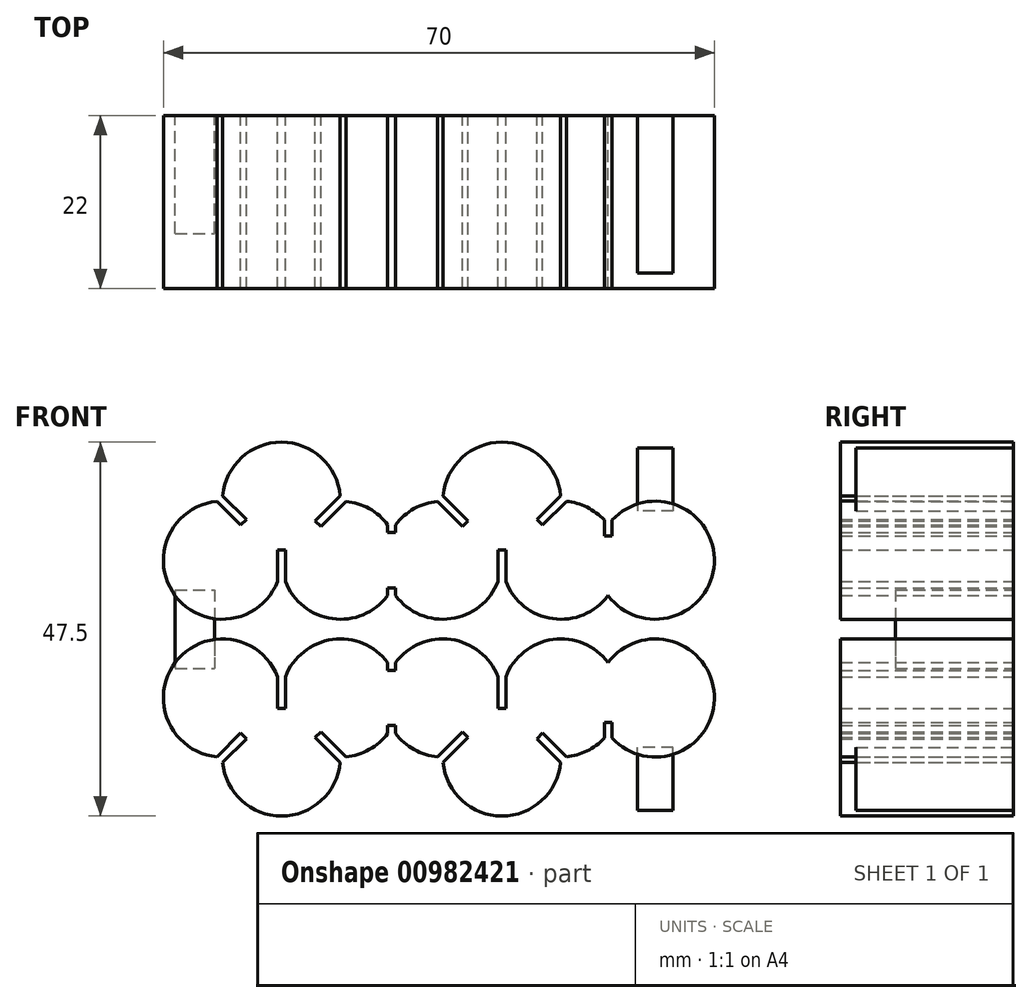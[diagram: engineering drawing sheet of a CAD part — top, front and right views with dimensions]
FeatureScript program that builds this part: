
annotation { "Feature Type Name" : "Feature", "Feature Type Description" : "" }
export const myFeature = defineFeature(function(context is Context, id is Id, definition is map)
    precondition{}
    {
        {
            var Q0;
            Q0=qCreatedBy(makeId("Front.planeOp"),FACE);
            var sketch = newSketch(context, id + "F0", { "sketchPlane" : qUnion([Q0])});
            skLineSegment(sketch, "E0.bottom", {"start": v(0, -25) * mm, "end": v(76, -25) * mm});
            skLineSegment(sketch, "E0.top", {"start": v(0, 25) * mm, "end": v(76, 25) * mm});
            skLineSegment(sketch, "E0.left", {"start": v(0, -25) * mm, "end": v(0, 25) * mm});
            skLineSegment(sketch, "E0.right", {"start": v(76, -25) * mm, "end": v(76, 25) * mm});
            skSolve(sketch);
        }
        {
            var Q0;
            Q0=makeQuery(id+"F0.imprint","IMPRINT",FACE,{"disambiguationData":[TD([[makeQuery(id+"F0.imprint","IMPRINT",EDGE,{"derivedFrom":sQuery(id+"F0.wireOp",EDGE,"E0.bottom")}),1.0]])]});
            var sketch = newSketch(context, id + "F1", { "sketchPlane" : qUnion([Q0])});
            skArc(sketch, "E1", {"start": v(10.03, -16.93) * mm, "mid": v(17.5, -23.75) * mm, "end": v(24.97, -16.93) * mm});
            skArc(sketch, "E2", {"start": v(25.68, -16.22) * mm, "mid": v(28.65, -15.3) * mm, "end": v(31, -13.25) * mm});
            skLineSegment(sketch, "E3.0", {"start": v(10.03, -16.93) * mm, "end": v(13.04, -13.92) * mm});
            skLineSegment(sketch, "E4.0", {"start": v(9.32, -16.22) * mm, "end": v(12.33, -13.21) * mm});
            skLineSegment(sketch, "E5.0", {"start": v(12.33, -13.21) * mm, "end": v(13.04, -13.92) * mm});
            skLineSegment(sketch, "E6.0", {"start": v(22.5, -13.04) * mm, "end": v(21.79, -13.74) * mm});
            skLineSegment(sketch, "E7.trimOffspring", {"start": v(21.79, -13.74) * mm, "end": v(24.97, -16.93) * mm});
            skLineSegment(sketch, "E8.trimOffspring", {"start": v(22.5, -13.04) * mm, "end": v(25.68, -16.22) * mm});
            skArc(sketch, "E9.trimOffspring", {"start": v(17, -6.06) * mm, "mid": v(4.02, -4.23) * mm, "end": v(9.32, -16.22) * mm});
            skLineSegment(sketch, "E10.0", {"start": v(18, -10.06) * mm, "end": v(18, -6.06) * mm});
            skLineSegment(sketch, "E11.0", {"start": v(17, -10.06) * mm, "end": v(17, -6.06) * mm});
            skLineSegment(sketch, "E12.0", {"start": v(17, -10.06) * mm, "end": v(18, -10.06) * mm});
            skArc(sketch, "E13", {"start": v(32, -13.25) * mm, "mid": v(34.35, -15.3) * mm, "end": v(37.32, -16.22) * mm});
            skLineSegment(sketch, "E14.0", {"start": v(31, -4.25) * mm, "end": v(31, -5.25) * mm});
            skLineSegment(sketch, "E15.0", {"start": v(32, -4.25) * mm, "end": v(32, -5.25) * mm});
            skArc(sketch, "E16.trimOffspring", {"start": v(31, -4.25) * mm, "mid": v(23.97, -1.32) * mm, "end": v(18, -6.06) * mm});
            skLineSegment(sketch, "E17.0", {"start": v(31, -5.25) * mm, "end": v(32, -5.25) * mm});
            skLineSegment(sketch, "E18.0", {"start": v(31, -12.25) * mm, "end": v(32, -12.25) * mm});
            skLineSegment(sketch, "E19.trimOffspring", {"start": v(31, -12.25) * mm, "end": v(31, -13.25) * mm});
            skLineSegment(sketch, "E20.trimOffspring", {"start": v(32, -12.25) * mm, "end": v(32, -13.25) * mm});
            skArc(sketch, "E21", {"start": v(38.03, -16.93) * mm, "mid": v(45.5, -23.75) * mm, "end": v(52.97, -16.93) * mm});
            skLineSegment(sketch, "E22.0", {"start": v(38.03, -16.93) * mm, "end": v(41.21, -13.74) * mm});
            skLineSegment(sketch, "E23.0", {"start": v(37.32, -16.22) * mm, "end": v(40.5, -13.04) * mm});
            skLineSegment(sketch, "E24.0", {"start": v(50.67, -13.21) * mm, "end": v(53.68, -16.22) * mm});
            skArc(sketch, "E25.trimOffspring", {"start": v(53.68, -16.22) * mm, "mid": v(56.3, -15.48) * mm, "end": v(58.5, -13.85) * mm});
            skArc(sketch, "E26.trimOffspring", {"start": v(45, -6.06) * mm, "mid": v(39.03, -1.32) * mm, "end": v(32, -4.25) * mm});
            skLineSegment(sketch, "E27.0", {"start": v(40.5, -13.04) * mm, "end": v(41.21, -13.74) * mm});
            skLineSegment(sketch, "E28.0", {"start": v(49.96, -13.92) * mm, "end": v(50.67, -13.21) * mm});
            skLineSegment(sketch, "E29.trimOffspring", {"start": v(49.96, -13.92) * mm, "end": v(52.97, -16.93) * mm});
            skLineSegment(sketch, "E30.0", {"start": v(46, -10.06) * mm, "end": v(46, -6.06) * mm});
            skLineSegment(sketch, "E31.0", {"start": v(45, -10.06) * mm, "end": v(45, -6.06) * mm});
            skLineSegment(sketch, "E32.0", {"start": v(45, -10.06) * mm, "end": v(46, -10.06) * mm});
            skArc(sketch, "E33", {"start": v(59.5, -13.85) * mm, "mid": v(72.49, -8.36) * mm, "end": v(59, -4.25) * mm});
            skLineSegment(sketch, "E34.0", {"start": v(59.5, -13.85) * mm, "end": v(59.5, -11.85) * mm});
            skLineSegment(sketch, "E35.0", {"start": v(58.5, -13.85) * mm, "end": v(58.5, -11.85) * mm});
            skLineSegment(sketch, "E36.0", {"start": v(58.5, -11.85) * mm, "end": v(59.5, -11.85) * mm});
            skArc(sketch, "E37.trimOffspring", {"start": v(59, -4.25) * mm, "mid": v(51.97, -1.32) * mm, "end": v(46, -6.06) * mm});
            skLineSegment(sketch, "E38.MirrorCS", {"start": v(31, 12.25) * mm, "end": v(32, 12.25) * mm});
            skLineSegment(sketch, "E39.MirrorCS", {"start": v(31, 5.25) * mm, "end": v(32, 5.25) * mm});
            skLineSegment(sketch, "E40.MirrorCS", {"start": v(49.96, 13.92) * mm, "end": v(50.67, 13.21) * mm});
            skLineSegment(sketch, "E41.MirrorCS", {"start": v(59.5, 13.85) * mm, "end": v(59.5, 11.85) * mm});
            skLineSegment(sketch, "E42.MirrorCS", {"start": v(12.33, 13.21) * mm, "end": v(13.04, 13.92) * mm});
            skLineSegment(sketch, "E43.MirrorCS", {"start": v(32, 12.25) * mm, "end": v(32, 13.25) * mm});
            skLineSegment(sketch, "E44.MirrorCS", {"start": v(22.5, 13.04) * mm, "end": v(21.79, 13.74) * mm});
            skLineSegment(sketch, "E45.MirrorCS", {"start": v(31, 12.25) * mm, "end": v(31, 13.25) * mm});
            skLineSegment(sketch, "E46.MirrorCS", {"start": v(58.5, 11.85) * mm, "end": v(59.5, 11.85) * mm});
            skLineSegment(sketch, "E47.MirrorCS", {"start": v(32, 4.25) * mm, "end": v(32, 5.25) * mm});
            skLineSegment(sketch, "E48.MirrorCS", {"start": v(17, 10.06) * mm, "end": v(18, 10.06) * mm});
            skLineSegment(sketch, "E49.MirrorCS", {"start": v(45, 10.06) * mm, "end": v(46, 10.06) * mm});
            skLineSegment(sketch, "E50.MirrorCS", {"start": v(58.5, 13.85) * mm, "end": v(58.5, 11.85) * mm});
            skLineSegment(sketch, "E51.MirrorCS", {"start": v(40.5, 13.04) * mm, "end": v(41.21, 13.74) * mm});
            skLineSegment(sketch, "E52.MirrorCS", {"start": v(31, 4.25) * mm, "end": v(31, 5.25) * mm});
            skLineSegment(sketch, "E53.MirrorCS", {"start": v(22.5, 13.04) * mm, "end": v(25.68, 16.22) * mm});
            skLineSegment(sketch, "E54.MirrorCS", {"start": v(45, 10.06) * mm, "end": v(45, 6.06) * mm});
            skArc(sketch, "E55.MirrorCS", {"start": v(38.03, 16.93) * mm, "mid": v(45.5, 23.75) * mm, "end": v(52.97, 16.93) * mm});
            skLineSegment(sketch, "E56.MirrorCS", {"start": v(17, 10.06) * mm, "end": v(17, 6.06) * mm});
            skArc(sketch, "E57.MirrorCS", {"start": v(45, 6.06) * mm, "mid": v(39.03, 1.32) * mm, "end": v(32, 4.25) * mm});
            skArc(sketch, "E58.MirrorCS", {"start": v(32, 13.25) * mm, "mid": v(34.35, 15.3) * mm, "end": v(37.32, 16.22) * mm});
            skArc(sketch, "E59.MirrorCS", {"start": v(17, 6.06) * mm, "mid": v(4.02, 4.23) * mm, "end": v(9.32, 16.22) * mm});
            skLineSegment(sketch, "E60.MirrorCS", {"start": v(18, 10.06) * mm, "end": v(18, 6.06) * mm});
            skLineSegment(sketch, "E61.MirrorCS", {"start": v(10.03, 16.93) * mm, "end": v(13.04, 13.92) * mm});
            skLineSegment(sketch, "E62.MirrorCS", {"start": v(21.79, 13.74) * mm, "end": v(24.97, 16.93) * mm});
            skLineSegment(sketch, "E63.MirrorCS", {"start": v(37.32, 16.22) * mm, "end": v(40.5, 13.04) * mm});
            skArc(sketch, "E64.MirrorCS", {"start": v(59.5, 13.85) * mm, "mid": v(72.49, 8.36) * mm, "end": v(59, 4.25) * mm});
            skLineSegment(sketch, "E65.MirrorCS", {"start": v(46, 10.06) * mm, "end": v(46, 6.06) * mm});
            skArc(sketch, "E66.MirrorCS", {"start": v(53.68, 16.22) * mm, "mid": v(56.3, 15.48) * mm, "end": v(58.5, 13.85) * mm});
            skLineSegment(sketch, "E67.MirrorCS", {"start": v(9.32, 16.22) * mm, "end": v(12.33, 13.21) * mm});
            skArc(sketch, "E68.MirrorCS", {"start": v(59, 4.25) * mm, "mid": v(51.97, 1.32) * mm, "end": v(46, 6.06) * mm});
            skArc(sketch, "E69.MirrorCS", {"start": v(25.68, 16.22) * mm, "mid": v(28.65, 15.3) * mm, "end": v(31, 13.25) * mm});
            skArc(sketch, "E70.MirrorCS", {"start": v(31, 4.25) * mm, "mid": v(23.97, 1.32) * mm, "end": v(18, 6.06) * mm});
            skLineSegment(sketch, "E71.MirrorCS", {"start": v(50.67, 13.21) * mm, "end": v(53.68, 16.22) * mm});
            skLineSegment(sketch, "E72.MirrorCS", {"start": v(49.96, 13.92) * mm, "end": v(52.97, 16.93) * mm});
            skLineSegment(sketch, "E73.MirrorCS", {"start": v(38.03, 16.93) * mm, "end": v(41.21, 13.74) * mm});
            skArc(sketch, "E74.MirrorCS", {"start": v(10.03, 16.93) * mm, "mid": v(17.5, 23.75) * mm, "end": v(24.97, 16.93) * mm});
            skSolve(sketch);
        }
        {
            var Q0;
            Q0 = qSketchRegion(id + "F1", true);
            extrude(context, id + "F2", {"entities" : qUnion([Q0]), "depth" : 22 * mm, "offsetDistance" : 25 * mm});
        }
        {
            var Q0;
            Q0=makeQuery(id+"F2.opExtrude","CAP_FACE",FACE,{"disambiguationData":[OSD([sQuery(id+"F1.wireOp",EDGE,"E1"),sQuery(id+"F1.wireOp",EDGE,"E2"),sQuery(id+"F1.wireOp",EDGE,"E3.0"),sQuery(id+"F1.wireOp",EDGE,"E4.0"),sQuery(id+"F1.wireOp",EDGE,"E5.0"),sQuery(id+"F1.wireOp",EDGE,"E6.0"),sQuery(id+"F1.wireOp",EDGE,"E7.trimOffspring"),sQuery(id+"F1.wireOp",EDGE,"E8.trimOffspring"),sQuery(id+"F1.wireOp",EDGE,"E9.trimOffspring"),sQuery(id+"F1.wireOp",EDGE,"E10.0"),sQuery(id+"F1.wireOp",EDGE,"E11.0"),sQuery(id+"F1.wireOp",EDGE,"E12.0"),sQuery(id+"F1.wireOp",EDGE,"E13"),sQuery(id+"F1.wireOp",EDGE,"E14.0"),sQuery(id+"F1.wireOp",EDGE,"E15.0"),sQuery(id+"F1.wireOp",EDGE,"E16.trimOffspring"),sQuery(id+"F1.wireOp",EDGE,"E17.0"),sQuery(id+"F1.wireOp",EDGE,"E18.0"),sQuery(id+"F1.wireOp",EDGE,"E19.trimOffspring"),sQuery(id+"F1.wireOp",EDGE,"E20.trimOffspring"),sQuery(id+"F1.wireOp",EDGE,"E21"),sQuery(id+"F1.wireOp",EDGE,"E22.0"),sQuery(id+"F1.wireOp",EDGE,"E23.0"),sQuery(id+"F1.wireOp",EDGE,"E24.0"),sQuery(id+"F1.wireOp",EDGE,"E25.trimOffspring"),sQuery(id+"F1.wireOp",EDGE,"E26.trimOffspring"),sQuery(id+"F1.wireOp",EDGE,"E27.0"),sQuery(id+"F1.wireOp",EDGE,"E28.0"),sQuery(id+"F1.wireOp",EDGE,"E29.trimOffspring"),sQuery(id+"F1.wireOp",EDGE,"E30.0"),sQuery(id+"F1.wireOp",EDGE,"E31.0"),sQuery(id+"F1.wireOp",EDGE,"E32.0"),sQuery(id+"F1.wireOp",EDGE,"E33"),sQuery(id+"F1.wireOp",EDGE,"E34.0"),sQuery(id+"F1.wireOp",EDGE,"E35.0"),sQuery(id+"F1.wireOp",EDGE,"E36.0"),sQuery(id+"F1.wireOp",EDGE,"E37.trimOffspring")])],"isStart":false});
            var sketch = newSketch(context, id + "F3", { "sketchPlane" : qUnion([Q0])});
            skCircle(sketch, "E75", {"center": v(10, -8.75) * mm, "radius": 2 * mm});
            skSolve(sketch);
        }
        {
            var Q0;
            Q0=makeQuery(id+"F3.imprint","IMPRINT",FACE,{"disambiguationData":[TD([[makeQuery(id+"F3.imprint","IMPRINT",EDGE,{"derivedFrom":sQuery(id+"F3.wireOp",EDGE,"E75")}),1.0]])]});
            var Q1;
            Q1=sQuery(id+"F3.wireOp",EDGE,"E75");
            extrude(context, id + "F4", {"entities" : qUnion([Q0]), "surfaceEntities" : qUnion([Q1]), "oppositeDirection" : true, "depth" : 21 * mm, "offsetDistance" : 25 * mm});
        }
        {
            var Q0;
            Q0=makeQuery(id+"F4.opExtrude","CAP_FACE",FACE,{"disambiguationData":[OSD([sQuery(id+"F3.wireOp",EDGE,"E75")])],"isStart":false});
            var sketch = newSketch(context, id + "F5", { "sketchPlane" : qUnion([Q0])});
            skCircle(sketch, "E76", {"center": v(-10, -8.75) * mm, "radius": 4 * mm});
            skSolve(sketch);
        }
        {
            var Q0;
            Q0 = qSketchRegion(id + "F5", true);
            extrude(context, id + "F6", {"entities" : qUnion([Q0]), "operationType" : NewBodyOperationType.ADD, "oppositeDirection" : true, "depth" : 1 * mm, "offsetDistance" : 25 * mm});
        }
        {
            var Q0;
            Q0=makeQuery(id+"F2.opExtrude","CAP_FACE",FACE,{"disambiguationData":[OSD([sQuery(id+"F1.wireOp",EDGE,"E1"),sQuery(id+"F1.wireOp",EDGE,"E2"),sQuery(id+"F1.wireOp",EDGE,"E3.0"),sQuery(id+"F1.wireOp",EDGE,"E4.0"),sQuery(id+"F1.wireOp",EDGE,"E5.0"),sQuery(id+"F1.wireOp",EDGE,"E6.0"),sQuery(id+"F1.wireOp",EDGE,"E7.trimOffspring"),sQuery(id+"F1.wireOp",EDGE,"E8.trimOffspring"),sQuery(id+"F1.wireOp",EDGE,"E9.trimOffspring"),sQuery(id+"F1.wireOp",EDGE,"E10.0"),sQuery(id+"F1.wireOp",EDGE,"E11.0"),sQuery(id+"F1.wireOp",EDGE,"E12.0"),sQuery(id+"F1.wireOp",EDGE,"E13"),sQuery(id+"F1.wireOp",EDGE,"E14.0"),sQuery(id+"F1.wireOp",EDGE,"E15.0"),sQuery(id+"F1.wireOp",EDGE,"E16.trimOffspring"),sQuery(id+"F1.wireOp",EDGE,"E17.0"),sQuery(id+"F1.wireOp",EDGE,"E18.0"),sQuery(id+"F1.wireOp",EDGE,"E19.trimOffspring"),sQuery(id+"F1.wireOp",EDGE,"E20.trimOffspring"),sQuery(id+"F1.wireOp",EDGE,"E21"),sQuery(id+"F1.wireOp",EDGE,"E22.0"),sQuery(id+"F1.wireOp",EDGE,"E23.0"),sQuery(id+"F1.wireOp",EDGE,"E24.0"),sQuery(id+"F1.wireOp",EDGE,"E25.trimOffspring"),sQuery(id+"F1.wireOp",EDGE,"E26.trimOffspring"),sQuery(id+"F1.wireOp",EDGE,"E27.0"),sQuery(id+"F1.wireOp",EDGE,"E28.0"),sQuery(id+"F1.wireOp",EDGE,"E29.trimOffspring"),sQuery(id+"F1.wireOp",EDGE,"E30.0"),sQuery(id+"F1.wireOp",EDGE,"E31.0"),sQuery(id+"F1.wireOp",EDGE,"E32.0"),sQuery(id+"F1.wireOp",EDGE,"E33"),sQuery(id+"F1.wireOp",EDGE,"E34.0"),sQuery(id+"F1.wireOp",EDGE,"E35.0"),sQuery(id+"F1.wireOp",EDGE,"E36.0"),sQuery(id+"F1.wireOp",EDGE,"E37.trimOffspring")])],"isStart":false});
            var sketch = newSketch(context, id + "F7", { "sketchPlane" : qUnion([Q0])});
            skCircle(sketch, "E77", {"center": v(17.5, -16.25) * mm, "radius": 2 * mm});
            skSolve(sketch);
        }
        {
            var Q0;
            Q0 = qSketchRegion(id + "F7", true);
            extrude(context, id + "F8", {"entities" : qUnion([Q0]), "oppositeDirection" : true, "depth" : 21 * mm, "offsetDistance" : 25 * mm});
        }
        {
            var Q0;
            Q0=makeQuery(id+"F8.opExtrude","CAP_FACE",FACE,{"disambiguationData":[OSD([sQuery(id+"F7.wireOp",EDGE,"E77")])],"isStart":false});
            var sketch = newSketch(context, id + "F9", { "sketchPlane" : qUnion([Q0])});
            skCircle(sketch, "E78", {"center": v(-17.5, -16.25) * mm, "radius": 4 * mm});
            skSolve(sketch);
        }
        {
            var Q0;
            Q0 = qSketchRegion(id + "F9", true);
            extrude(context, id + "F10", {"entities" : qUnion([Q0]), "operationType" : NewBodyOperationType.ADD, "oppositeDirection" : true, "depth" : 1 * mm, "offsetDistance" : 25 * mm});
        }
        {
            var Q0;
            Q0=makeQuery(id+"F2.opExtrude","CAP_FACE",FACE,{"disambiguationData":[OSD([sQuery(id+"F1.wireOp",EDGE,"E1"),sQuery(id+"F1.wireOp",EDGE,"E2"),sQuery(id+"F1.wireOp",EDGE,"E3.0"),sQuery(id+"F1.wireOp",EDGE,"E4.0"),sQuery(id+"F1.wireOp",EDGE,"E5.0"),sQuery(id+"F1.wireOp",EDGE,"E6.0"),sQuery(id+"F1.wireOp",EDGE,"E7.trimOffspring"),sQuery(id+"F1.wireOp",EDGE,"E8.trimOffspring"),sQuery(id+"F1.wireOp",EDGE,"E9.trimOffspring"),sQuery(id+"F1.wireOp",EDGE,"E10.0"),sQuery(id+"F1.wireOp",EDGE,"E11.0"),sQuery(id+"F1.wireOp",EDGE,"E12.0"),sQuery(id+"F1.wireOp",EDGE,"E13"),sQuery(id+"F1.wireOp",EDGE,"E14.0"),sQuery(id+"F1.wireOp",EDGE,"E15.0"),sQuery(id+"F1.wireOp",EDGE,"E16.trimOffspring"),sQuery(id+"F1.wireOp",EDGE,"E17.0"),sQuery(id+"F1.wireOp",EDGE,"E18.0"),sQuery(id+"F1.wireOp",EDGE,"E19.trimOffspring"),sQuery(id+"F1.wireOp",EDGE,"E20.trimOffspring"),sQuery(id+"F1.wireOp",EDGE,"E21"),sQuery(id+"F1.wireOp",EDGE,"E22.0"),sQuery(id+"F1.wireOp",EDGE,"E23.0"),sQuery(id+"F1.wireOp",EDGE,"E24.0"),sQuery(id+"F1.wireOp",EDGE,"E25.trimOffspring"),sQuery(id+"F1.wireOp",EDGE,"E26.trimOffspring"),sQuery(id+"F1.wireOp",EDGE,"E27.0"),sQuery(id+"F1.wireOp",EDGE,"E28.0"),sQuery(id+"F1.wireOp",EDGE,"E29.trimOffspring"),sQuery(id+"F1.wireOp",EDGE,"E30.0"),sQuery(id+"F1.wireOp",EDGE,"E31.0"),sQuery(id+"F1.wireOp",EDGE,"E32.0"),sQuery(id+"F1.wireOp",EDGE,"E33"),sQuery(id+"F1.wireOp",EDGE,"E34.0"),sQuery(id+"F1.wireOp",EDGE,"E35.0"),sQuery(id+"F1.wireOp",EDGE,"E36.0"),sQuery(id+"F1.wireOp",EDGE,"E37.trimOffspring")])],"isStart":false});
            var sketch = newSketch(context, id + "F11", { "sketchPlane" : qUnion([Q0])});
            skCircle(sketch, "E79", {"center": v(25, -8.75) * mm, "radius": 2 * mm});
            skSolve(sketch);
        }
        {
            var Q0;
            Q0=makeQuery(id+"F11.imprint","IMPRINT",FACE,{"disambiguationData":[TD([[makeQuery(id+"F11.imprint","IMPRINT",EDGE,{"derivedFrom":sQuery(id+"F11.wireOp",EDGE,"E79")}),1.0]])]});
            var Q1;
            Q1=sQuery(id+"F11.wireOp",EDGE,"E79");
            extrude(context, id + "F12", {"entities" : qUnion([Q0]), "operationType" : NewBodyOperationType.ADD, "surfaceEntities" : qUnion([Q1]), "oppositeDirection" : true, "depth" : 21 * mm, "offsetDistance" : 25 * mm});
        }
        {
            var Q0;
            Q0=makeQuery(id+"F2.opExtrude","CAP_FACE",FACE,{"disambiguationData":[OSD([sQuery(id+"F1.wireOp",EDGE,"E1"),sQuery(id+"F1.wireOp",EDGE,"E2"),sQuery(id+"F1.wireOp",EDGE,"E3.0"),sQuery(id+"F1.wireOp",EDGE,"E4.0"),sQuery(id+"F1.wireOp",EDGE,"E5.0"),sQuery(id+"F1.wireOp",EDGE,"E6.0"),sQuery(id+"F1.wireOp",EDGE,"E7.trimOffspring"),sQuery(id+"F1.wireOp",EDGE,"E8.trimOffspring"),sQuery(id+"F1.wireOp",EDGE,"E9.trimOffspring"),sQuery(id+"F1.wireOp",EDGE,"E10.0"),sQuery(id+"F1.wireOp",EDGE,"E11.0"),sQuery(id+"F1.wireOp",EDGE,"E12.0"),sQuery(id+"F1.wireOp",EDGE,"E13"),sQuery(id+"F1.wireOp",EDGE,"E14.0"),sQuery(id+"F1.wireOp",EDGE,"E15.0"),sQuery(id+"F1.wireOp",EDGE,"E16.trimOffspring"),sQuery(id+"F1.wireOp",EDGE,"E17.0"),sQuery(id+"F1.wireOp",EDGE,"E18.0"),sQuery(id+"F1.wireOp",EDGE,"E19.trimOffspring"),sQuery(id+"F1.wireOp",EDGE,"E20.trimOffspring"),sQuery(id+"F1.wireOp",EDGE,"E21"),sQuery(id+"F1.wireOp",EDGE,"E22.0"),sQuery(id+"F1.wireOp",EDGE,"E23.0"),sQuery(id+"F1.wireOp",EDGE,"E24.0"),sQuery(id+"F1.wireOp",EDGE,"E25.trimOffspring"),sQuery(id+"F1.wireOp",EDGE,"E26.trimOffspring"),sQuery(id+"F1.wireOp",EDGE,"E27.0"),sQuery(id+"F1.wireOp",EDGE,"E28.0"),sQuery(id+"F1.wireOp",EDGE,"E29.trimOffspring"),sQuery(id+"F1.wireOp",EDGE,"E30.0"),sQuery(id+"F1.wireOp",EDGE,"E31.0"),sQuery(id+"F1.wireOp",EDGE,"E32.0"),sQuery(id+"F1.wireOp",EDGE,"E33"),sQuery(id+"F1.wireOp",EDGE,"E34.0"),sQuery(id+"F1.wireOp",EDGE,"E35.0"),sQuery(id+"F1.wireOp",EDGE,"E36.0"),sQuery(id+"F1.wireOp",EDGE,"E37.trimOffspring")])],"isStart":false});
            var sketch = newSketch(context, id + "F13", { "sketchPlane" : qUnion([Q0])});
            skCircle(sketch, "E80", {"center": v(25, -8.75) * mm, "radius": 2 * mm});
            skSolve(sketch);
        }
        {
            var Q0;
            Q0 = qSketchRegion(id + "F13", true);
            extrude(context, id + "F14", {"entities" : qUnion([Q0]), "oppositeDirection" : true, "depth" : 21 * mm, "offsetDistance" : 25 * mm});
        }
        {
            var Q0;
            Q0=makeQuery(id+"F14.opExtrude","CAP_FACE",FACE,{"disambiguationData":[OSD([sQuery(id+"F13.wireOp",EDGE,"E80")])],"isStart":false});
            var sketch = newSketch(context, id + "F15", { "sketchPlane" : qUnion([Q0])});
            skCircle(sketch, "E81", {"center": v(-25, -8.75) * mm, "radius": 4 * mm});
            skSolve(sketch);
        }
        {
            var Q0;
            Q0 = qSketchRegion(id + "F15", true);
            extrude(context, id + "F16", {"entities" : qUnion([Q0]), "operationType" : NewBodyOperationType.ADD, "oppositeDirection" : true, "depth" : 1 * mm, "offsetDistance" : 25 * mm});
        }
        {
            var Q0;
            Q0=makeQuery(id+"F2.opExtrude","CAP_FACE",FACE,{"disambiguationData":[OSD([sQuery(id+"F1.wireOp",EDGE,"E1"),sQuery(id+"F1.wireOp",EDGE,"E2"),sQuery(id+"F1.wireOp",EDGE,"E3.0"),sQuery(id+"F1.wireOp",EDGE,"E4.0"),sQuery(id+"F1.wireOp",EDGE,"E5.0"),sQuery(id+"F1.wireOp",EDGE,"E6.0"),sQuery(id+"F1.wireOp",EDGE,"E7.trimOffspring"),sQuery(id+"F1.wireOp",EDGE,"E8.trimOffspring"),sQuery(id+"F1.wireOp",EDGE,"E9.trimOffspring"),sQuery(id+"F1.wireOp",EDGE,"E10.0"),sQuery(id+"F1.wireOp",EDGE,"E11.0"),sQuery(id+"F1.wireOp",EDGE,"E12.0"),sQuery(id+"F1.wireOp",EDGE,"E13"),sQuery(id+"F1.wireOp",EDGE,"E14.0"),sQuery(id+"F1.wireOp",EDGE,"E15.0"),sQuery(id+"F1.wireOp",EDGE,"E16.trimOffspring"),sQuery(id+"F1.wireOp",EDGE,"E17.0"),sQuery(id+"F1.wireOp",EDGE,"E18.0"),sQuery(id+"F1.wireOp",EDGE,"E19.trimOffspring"),sQuery(id+"F1.wireOp",EDGE,"E20.trimOffspring"),sQuery(id+"F1.wireOp",EDGE,"E21"),sQuery(id+"F1.wireOp",EDGE,"E22.0"),sQuery(id+"F1.wireOp",EDGE,"E23.0"),sQuery(id+"F1.wireOp",EDGE,"E24.0"),sQuery(id+"F1.wireOp",EDGE,"E25.trimOffspring"),sQuery(id+"F1.wireOp",EDGE,"E26.trimOffspring"),sQuery(id+"F1.wireOp",EDGE,"E27.0"),sQuery(id+"F1.wireOp",EDGE,"E28.0"),sQuery(id+"F1.wireOp",EDGE,"E29.trimOffspring"),sQuery(id+"F1.wireOp",EDGE,"E30.0"),sQuery(id+"F1.wireOp",EDGE,"E31.0"),sQuery(id+"F1.wireOp",EDGE,"E32.0"),sQuery(id+"F1.wireOp",EDGE,"E33"),sQuery(id+"F1.wireOp",EDGE,"E34.0"),sQuery(id+"F1.wireOp",EDGE,"E35.0"),sQuery(id+"F1.wireOp",EDGE,"E36.0"),sQuery(id+"F1.wireOp",EDGE,"E37.trimOffspring")])],"isStart":false});
            var sketch = newSketch(context, id + "F17", { "sketchPlane" : qUnion([Q0])});
            skCircle(sketch, "E82", {"center": v(38, -8.75) * mm, "radius": 2 * mm});
            skSolve(sketch);
        }
        {
            var Q0;
            Q0 = qSketchRegion(id + "F17", true);
            extrude(context, id + "F18", {"entities" : qUnion([Q0]), "oppositeDirection" : true, "depth" : 21 * mm, "offsetDistance" : 25 * mm});
        }
        {
            var Q0;
            Q0=makeQuery(id+"F18.opExtrude","CAP_FACE",FACE,{"disambiguationData":[OSD([sQuery(id+"F17.wireOp",EDGE,"E82")])],"isStart":false});
            var sketch = newSketch(context, id + "F19", { "sketchPlane" : qUnion([Q0])});
            skCircle(sketch, "E83", {"center": v(-38, -8.75) * mm, "radius": 4 * mm});
            skSolve(sketch);
        }
        {
            var Q0;
            Q0 = qSketchRegion(id + "F19", true);
            extrude(context, id + "F20", {"entities" : qUnion([Q0]), "operationType" : NewBodyOperationType.ADD, "oppositeDirection" : true, "depth" : 1 * mm, "offsetDistance" : 25 * mm});
        }
        {
            var Q0;
            Q0=makeQuery(id+"F2.opExtrude","CAP_FACE",FACE,{"disambiguationData":[OSD([sQuery(id+"F1.wireOp",EDGE,"E1"),sQuery(id+"F1.wireOp",EDGE,"E2"),sQuery(id+"F1.wireOp",EDGE,"E3.0"),sQuery(id+"F1.wireOp",EDGE,"E4.0"),sQuery(id+"F1.wireOp",EDGE,"E5.0"),sQuery(id+"F1.wireOp",EDGE,"E6.0"),sQuery(id+"F1.wireOp",EDGE,"E7.trimOffspring"),sQuery(id+"F1.wireOp",EDGE,"E8.trimOffspring"),sQuery(id+"F1.wireOp",EDGE,"E9.trimOffspring"),sQuery(id+"F1.wireOp",EDGE,"E10.0"),sQuery(id+"F1.wireOp",EDGE,"E11.0"),sQuery(id+"F1.wireOp",EDGE,"E12.0"),sQuery(id+"F1.wireOp",EDGE,"E13"),sQuery(id+"F1.wireOp",EDGE,"E14.0"),sQuery(id+"F1.wireOp",EDGE,"E15.0"),sQuery(id+"F1.wireOp",EDGE,"E16.trimOffspring"),sQuery(id+"F1.wireOp",EDGE,"E17.0"),sQuery(id+"F1.wireOp",EDGE,"E18.0"),sQuery(id+"F1.wireOp",EDGE,"E19.trimOffspring"),sQuery(id+"F1.wireOp",EDGE,"E20.trimOffspring"),sQuery(id+"F1.wireOp",EDGE,"E21"),sQuery(id+"F1.wireOp",EDGE,"E22.0"),sQuery(id+"F1.wireOp",EDGE,"E23.0"),sQuery(id+"F1.wireOp",EDGE,"E24.0"),sQuery(id+"F1.wireOp",EDGE,"E25.trimOffspring"),sQuery(id+"F1.wireOp",EDGE,"E26.trimOffspring"),sQuery(id+"F1.wireOp",EDGE,"E27.0"),sQuery(id+"F1.wireOp",EDGE,"E28.0"),sQuery(id+"F1.wireOp",EDGE,"E29.trimOffspring"),sQuery(id+"F1.wireOp",EDGE,"E30.0"),sQuery(id+"F1.wireOp",EDGE,"E31.0"),sQuery(id+"F1.wireOp",EDGE,"E32.0"),sQuery(id+"F1.wireOp",EDGE,"E33"),sQuery(id+"F1.wireOp",EDGE,"E34.0"),sQuery(id+"F1.wireOp",EDGE,"E35.0"),sQuery(id+"F1.wireOp",EDGE,"E36.0"),sQuery(id+"F1.wireOp",EDGE,"E37.trimOffspring")])],"isStart":false});
            var sketch = newSketch(context, id + "F21", { "sketchPlane" : qUnion([Q0])});
            skCircle(sketch, "E84", {"center": v(45.5, -16.25) * mm, "radius": 2 * mm});
            skSolve(sketch);
        }
        {
            var Q0;
            Q0 = qSketchRegion(id + "F21", true);
            extrude(context, id + "F22", {"entities" : qUnion([Q0]), "oppositeDirection" : true, "depth" : 21 * mm, "offsetDistance" : 25 * mm});
        }
        {
            var Q0;
            Q0=makeQuery(id+"F22.opExtrude","CAP_FACE",FACE,{"disambiguationData":[OSD([sQuery(id+"F21.wireOp",EDGE,"E84")])],"isStart":false});
            var sketch = newSketch(context, id + "F23", { "sketchPlane" : qUnion([Q0])});
            skCircle(sketch, "E85", {"center": v(-45.5, -16.25) * mm, "radius": 4 * mm});
            skSolve(sketch);
        }
        {
            var Q0;
            Q0=makeQuery(id+"F23.imprint","IMPRINT",FACE,{"disambiguationData":[TD([[makeQuery(id+"F23.imprint","IMPRINT",EDGE,{"derivedFrom":sQuery(id+"F23.wireOp",EDGE,"E85")}),1.0]])]});
            extrude(context, id + "F24", {"entities" : qUnion([Q0]), "operationType" : NewBodyOperationType.ADD, "oppositeDirection" : true, "depth" : 1 * mm, "offsetDistance" : 25 * mm});
        }
        {
            var Q0;
            Q0=makeQuery(id+"F2.opExtrude","CAP_FACE",FACE,{"disambiguationData":[OSD([sQuery(id+"F1.wireOp",EDGE,"E1"),sQuery(id+"F1.wireOp",EDGE,"E2"),sQuery(id+"F1.wireOp",EDGE,"E3.0"),sQuery(id+"F1.wireOp",EDGE,"E4.0"),sQuery(id+"F1.wireOp",EDGE,"E5.0"),sQuery(id+"F1.wireOp",EDGE,"E6.0"),sQuery(id+"F1.wireOp",EDGE,"E7.trimOffspring"),sQuery(id+"F1.wireOp",EDGE,"E8.trimOffspring"),sQuery(id+"F1.wireOp",EDGE,"E9.trimOffspring"),sQuery(id+"F1.wireOp",EDGE,"E10.0"),sQuery(id+"F1.wireOp",EDGE,"E11.0"),sQuery(id+"F1.wireOp",EDGE,"E12.0"),sQuery(id+"F1.wireOp",EDGE,"E13"),sQuery(id+"F1.wireOp",EDGE,"E14.0"),sQuery(id+"F1.wireOp",EDGE,"E15.0"),sQuery(id+"F1.wireOp",EDGE,"E16.trimOffspring"),sQuery(id+"F1.wireOp",EDGE,"E17.0"),sQuery(id+"F1.wireOp",EDGE,"E18.0"),sQuery(id+"F1.wireOp",EDGE,"E19.trimOffspring"),sQuery(id+"F1.wireOp",EDGE,"E20.trimOffspring"),sQuery(id+"F1.wireOp",EDGE,"E21"),sQuery(id+"F1.wireOp",EDGE,"E22.0"),sQuery(id+"F1.wireOp",EDGE,"E23.0"),sQuery(id+"F1.wireOp",EDGE,"E24.0"),sQuery(id+"F1.wireOp",EDGE,"E25.trimOffspring"),sQuery(id+"F1.wireOp",EDGE,"E26.trimOffspring"),sQuery(id+"F1.wireOp",EDGE,"E27.0"),sQuery(id+"F1.wireOp",EDGE,"E28.0"),sQuery(id+"F1.wireOp",EDGE,"E29.trimOffspring"),sQuery(id+"F1.wireOp",EDGE,"E30.0"),sQuery(id+"F1.wireOp",EDGE,"E31.0"),sQuery(id+"F1.wireOp",EDGE,"E32.0"),sQuery(id+"F1.wireOp",EDGE,"E33"),sQuery(id+"F1.wireOp",EDGE,"E34.0"),sQuery(id+"F1.wireOp",EDGE,"E35.0"),sQuery(id+"F1.wireOp",EDGE,"E36.0"),sQuery(id+"F1.wireOp",EDGE,"E37.trimOffspring")])],"isStart":false});
            var sketch = newSketch(context, id + "F25", { "sketchPlane" : qUnion([Q0])});
            skCircle(sketch, "E86", {"center": v(53, -8.75) * mm, "radius": 2 * mm});
            skSolve(sketch);
        }
        {
            var Q0;
            Q0 = qSketchRegion(id + "F25", true);
            extrude(context, id + "F26", {"entities" : qUnion([Q0]), "oppositeDirection" : true, "depth" : 21 * mm, "offsetDistance" : 25 * mm});
        }
        {
            var Q0;
            Q0=makeQuery(id+"F26.opExtrude","CAP_FACE",FACE,{"disambiguationData":[OSD([sQuery(id+"F25.wireOp",EDGE,"E86")])],"isStart":false});
            var sketch = newSketch(context, id + "F27", { "sketchPlane" : qUnion([Q0])});
            skCircle(sketch, "E87", {"center": v(-53, -8.75) * mm, "radius": 4 * mm});
            skSolve(sketch);
        }
        {
            var Q0;
            Q0=makeQuery(id+"F27.imprint","IMPRINT",FACE,{"disambiguationData":[TD([[makeQuery(id+"F27.imprint","IMPRINT",EDGE,{"derivedFrom":sQuery(id+"F27.wireOp",EDGE,"E87")}),1.0]])]});
            extrude(context, id + "F28", {"entities" : qUnion([Q0]), "operationType" : NewBodyOperationType.ADD, "oppositeDirection" : true, "depth" : 1 * mm, "offsetDistance" : 25 * mm});
        }
        {
            var Q0;
            Q0=makeQuery(id+"F2.opExtrude","CAP_FACE",FACE,{"disambiguationData":[OSD([sQuery(id+"F1.wireOp",EDGE,"E1"),sQuery(id+"F1.wireOp",EDGE,"E2"),sQuery(id+"F1.wireOp",EDGE,"E3.0"),sQuery(id+"F1.wireOp",EDGE,"E4.0"),sQuery(id+"F1.wireOp",EDGE,"E5.0"),sQuery(id+"F1.wireOp",EDGE,"E6.0"),sQuery(id+"F1.wireOp",EDGE,"E7.trimOffspring"),sQuery(id+"F1.wireOp",EDGE,"E8.trimOffspring"),sQuery(id+"F1.wireOp",EDGE,"E9.trimOffspring"),sQuery(id+"F1.wireOp",EDGE,"E10.0"),sQuery(id+"F1.wireOp",EDGE,"E11.0"),sQuery(id+"F1.wireOp",EDGE,"E12.0"),sQuery(id+"F1.wireOp",EDGE,"E13"),sQuery(id+"F1.wireOp",EDGE,"E14.0"),sQuery(id+"F1.wireOp",EDGE,"E15.0"),sQuery(id+"F1.wireOp",EDGE,"E16.trimOffspring"),sQuery(id+"F1.wireOp",EDGE,"E17.0"),sQuery(id+"F1.wireOp",EDGE,"E18.0"),sQuery(id+"F1.wireOp",EDGE,"E19.trimOffspring"),sQuery(id+"F1.wireOp",EDGE,"E20.trimOffspring"),sQuery(id+"F1.wireOp",EDGE,"E21"),sQuery(id+"F1.wireOp",EDGE,"E22.0"),sQuery(id+"F1.wireOp",EDGE,"E23.0"),sQuery(id+"F1.wireOp",EDGE,"E24.0"),sQuery(id+"F1.wireOp",EDGE,"E25.trimOffspring"),sQuery(id+"F1.wireOp",EDGE,"E26.trimOffspring"),sQuery(id+"F1.wireOp",EDGE,"E27.0"),sQuery(id+"F1.wireOp",EDGE,"E28.0"),sQuery(id+"F1.wireOp",EDGE,"E29.trimOffspring"),sQuery(id+"F1.wireOp",EDGE,"E30.0"),sQuery(id+"F1.wireOp",EDGE,"E31.0"),sQuery(id+"F1.wireOp",EDGE,"E32.0"),sQuery(id+"F1.wireOp",EDGE,"E33"),sQuery(id+"F1.wireOp",EDGE,"E34.0"),sQuery(id+"F1.wireOp",EDGE,"E35.0"),sQuery(id+"F1.wireOp",EDGE,"E36.0"),sQuery(id+"F1.wireOp",EDGE,"E37.trimOffspring")])],"isStart":false});
            var sketch = newSketch(context, id + "F29", { "sketchPlane" : qUnion([Q0])});
            skCircle(sketch, "E88", {"center": v(65, -8.75) * mm, "radius": 2 * mm});
            skSolve(sketch);
        }
        {
            var Q0;
            Q0 = qSketchRegion(id + "F29", true);
            extrude(context, id + "F30", {"entities" : qUnion([Q0]), "oppositeDirection" : true, "depth" : 21 * mm, "offsetDistance" : 25 * mm});
        }
        {
            var Q0;
            Q0=makeQuery(id+"F30.opExtrude","CAP_FACE",FACE,{"disambiguationData":[OSD([sQuery(id+"F29.wireOp",EDGE,"E88")])],"isStart":false});
            var sketch = newSketch(context, id + "F31", { "sketchPlane" : qUnion([Q0])});
            skCircle(sketch, "E89", {"center": v(-65, -8.75) * mm, "radius": 4 * mm});
            skSolve(sketch);
        }
        {
            var Q0;
            Q0=makeQuery(id+"F31.imprint","IMPRINT",FACE,{"disambiguationData":[TD([[makeQuery(id+"F31.imprint","IMPRINT",EDGE,{"derivedFrom":sQuery(id+"F31.wireOp",EDGE,"E89")}),1.0]])]});
            var Q1;
            Q1=sQuery(id+"F31.wireOp",EDGE,"E89");
            extrude(context, id + "F32", {"entities" : qUnion([Q0]), "operationType" : NewBodyOperationType.ADD, "surfaceOperationType" : NewSurfaceOperationType.ADD, "surfaceEntities" : qUnion([Q1]), "oppositeDirection" : true, "depth" : 1 * mm, "offsetDistance" : 25 * mm});
        }
        {
            var Q0;
            Q0=makeQuery(id+"F2.opExtrude","CAP_FACE",FACE,{"disambiguationData":[OSD([sQuery(id+"F1.wireOp",EDGE,"E38.MirrorCS"),sQuery(id+"F1.wireOp",EDGE,"E39.MirrorCS"),sQuery(id+"F1.wireOp",EDGE,"E40.MirrorCS"),sQuery(id+"F1.wireOp",EDGE,"E41.MirrorCS"),sQuery(id+"F1.wireOp",EDGE,"E42.MirrorCS"),sQuery(id+"F1.wireOp",EDGE,"E43.MirrorCS"),sQuery(id+"F1.wireOp",EDGE,"E44.MirrorCS"),sQuery(id+"F1.wireOp",EDGE,"E45.MirrorCS"),sQuery(id+"F1.wireOp",EDGE,"E46.MirrorCS"),sQuery(id+"F1.wireOp",EDGE,"E47.MirrorCS"),sQuery(id+"F1.wireOp",EDGE,"E48.MirrorCS"),sQuery(id+"F1.wireOp",EDGE,"E49.MirrorCS"),sQuery(id+"F1.wireOp",EDGE,"E50.MirrorCS"),sQuery(id+"F1.wireOp",EDGE,"E51.MirrorCS"),sQuery(id+"F1.wireOp",EDGE,"E52.MirrorCS"),sQuery(id+"F1.wireOp",EDGE,"E53.MirrorCS"),sQuery(id+"F1.wireOp",EDGE,"E54.MirrorCS"),sQuery(id+"F1.wireOp",EDGE,"E55.MirrorCS"),sQuery(id+"F1.wireOp",EDGE,"E56.MirrorCS"),sQuery(id+"F1.wireOp",EDGE,"E57.MirrorCS"),sQuery(id+"F1.wireOp",EDGE,"E58.MirrorCS"),sQuery(id+"F1.wireOp",EDGE,"E59.MirrorCS"),sQuery(id+"F1.wireOp",EDGE,"E60.MirrorCS"),sQuery(id+"F1.wireOp",EDGE,"E61.MirrorCS"),sQuery(id+"F1.wireOp",EDGE,"E62.MirrorCS"),sQuery(id+"F1.wireOp",EDGE,"E63.MirrorCS"),sQuery(id+"F1.wireOp",EDGE,"E64.MirrorCS"),sQuery(id+"F1.wireOp",EDGE,"E65.MirrorCS"),sQuery(id+"F1.wireOp",EDGE,"E66.MirrorCS"),sQuery(id+"F1.wireOp",EDGE,"E67.MirrorCS"),sQuery(id+"F1.wireOp",EDGE,"E68.MirrorCS"),sQuery(id+"F1.wireOp",EDGE,"E69.MirrorCS"),sQuery(id+"F1.wireOp",EDGE,"E70.MirrorCS"),sQuery(id+"F1.wireOp",EDGE,"E71.MirrorCS"),sQuery(id+"F1.wireOp",EDGE,"E72.MirrorCS"),sQuery(id+"F1.wireOp",EDGE,"E73.MirrorCS"),sQuery(id+"F1.wireOp",EDGE,"E74.MirrorCS")])],"isStart":false});
            var sketch = newSketch(context, id + "F33", { "sketchPlane" : qUnion([Q0])});
            skCircle(sketch, "E90", {"center": v(10, 8.75) * mm, "radius": 2 * mm});
            skSolve(sketch);
        }
        {
            var Q0;
            Q0 = qSketchRegion(id + "F33", true);
            extrude(context, id + "F34", {"entities" : qUnion([Q0]), "oppositeDirection" : true, "depth" : 20 * mm, "offsetDistance" : 25 * mm});
        }
        {
            var Q0;
            Q0=makeQuery(id+"F2.opExtrude","CAP_FACE",FACE,{"disambiguationData":[OSD([sQuery(id+"F1.wireOp",EDGE,"E38.MirrorCS"),sQuery(id+"F1.wireOp",EDGE,"E39.MirrorCS"),sQuery(id+"F1.wireOp",EDGE,"E40.MirrorCS"),sQuery(id+"F1.wireOp",EDGE,"E41.MirrorCS"),sQuery(id+"F1.wireOp",EDGE,"E42.MirrorCS"),sQuery(id+"F1.wireOp",EDGE,"E43.MirrorCS"),sQuery(id+"F1.wireOp",EDGE,"E44.MirrorCS"),sQuery(id+"F1.wireOp",EDGE,"E45.MirrorCS"),sQuery(id+"F1.wireOp",EDGE,"E46.MirrorCS"),sQuery(id+"F1.wireOp",EDGE,"E47.MirrorCS"),sQuery(id+"F1.wireOp",EDGE,"E48.MirrorCS"),sQuery(id+"F1.wireOp",EDGE,"E49.MirrorCS"),sQuery(id+"F1.wireOp",EDGE,"E50.MirrorCS"),sQuery(id+"F1.wireOp",EDGE,"E51.MirrorCS"),sQuery(id+"F1.wireOp",EDGE,"E52.MirrorCS"),sQuery(id+"F1.wireOp",EDGE,"E53.MirrorCS"),sQuery(id+"F1.wireOp",EDGE,"E54.MirrorCS"),sQuery(id+"F1.wireOp",EDGE,"E55.MirrorCS"),sQuery(id+"F1.wireOp",EDGE,"E56.MirrorCS"),sQuery(id+"F1.wireOp",EDGE,"E57.MirrorCS"),sQuery(id+"F1.wireOp",EDGE,"E58.MirrorCS"),sQuery(id+"F1.wireOp",EDGE,"E59.MirrorCS"),sQuery(id+"F1.wireOp",EDGE,"E60.MirrorCS"),sQuery(id+"F1.wireOp",EDGE,"E61.MirrorCS"),sQuery(id+"F1.wireOp",EDGE,"E62.MirrorCS"),sQuery(id+"F1.wireOp",EDGE,"E63.MirrorCS"),sQuery(id+"F1.wireOp",EDGE,"E64.MirrorCS"),sQuery(id+"F1.wireOp",EDGE,"E65.MirrorCS"),sQuery(id+"F1.wireOp",EDGE,"E66.MirrorCS"),sQuery(id+"F1.wireOp",EDGE,"E67.MirrorCS"),sQuery(id+"F1.wireOp",EDGE,"E68.MirrorCS"),sQuery(id+"F1.wireOp",EDGE,"E69.MirrorCS"),sQuery(id+"F1.wireOp",EDGE,"E70.MirrorCS"),sQuery(id+"F1.wireOp",EDGE,"E71.MirrorCS"),sQuery(id+"F1.wireOp",EDGE,"E72.MirrorCS"),sQuery(id+"F1.wireOp",EDGE,"E73.MirrorCS"),sQuery(id+"F1.wireOp",EDGE,"E74.MirrorCS")])],"isStart":false});
            var sketch = newSketch(context, id + "F35", { "sketchPlane" : qUnion([Q0])});
            skCircle(sketch, "E91", {"center": v(17.5, 16.25) * mm, "radius": 2 * mm});
            skSolve(sketch);
        }
        {
            var Q0;
            Q0 = qSketchRegion(id + "F35", true);
            extrude(context, id + "F36", {"entities" : qUnion([Q0]), "oppositeDirection" : true, "depth" : 20 * mm, "offsetDistance" : 25 * mm});
        }
        {
            var Q0;
            Q0=makeQuery(id+"F2.opExtrude","CAP_FACE",FACE,{"disambiguationData":[OSD([sQuery(id+"F1.wireOp",EDGE,"E38.MirrorCS"),sQuery(id+"F1.wireOp",EDGE,"E39.MirrorCS"),sQuery(id+"F1.wireOp",EDGE,"E40.MirrorCS"),sQuery(id+"F1.wireOp",EDGE,"E41.MirrorCS"),sQuery(id+"F1.wireOp",EDGE,"E42.MirrorCS"),sQuery(id+"F1.wireOp",EDGE,"E43.MirrorCS"),sQuery(id+"F1.wireOp",EDGE,"E44.MirrorCS"),sQuery(id+"F1.wireOp",EDGE,"E45.MirrorCS"),sQuery(id+"F1.wireOp",EDGE,"E46.MirrorCS"),sQuery(id+"F1.wireOp",EDGE,"E47.MirrorCS"),sQuery(id+"F1.wireOp",EDGE,"E48.MirrorCS"),sQuery(id+"F1.wireOp",EDGE,"E49.MirrorCS"),sQuery(id+"F1.wireOp",EDGE,"E50.MirrorCS"),sQuery(id+"F1.wireOp",EDGE,"E51.MirrorCS"),sQuery(id+"F1.wireOp",EDGE,"E52.MirrorCS"),sQuery(id+"F1.wireOp",EDGE,"E53.MirrorCS"),sQuery(id+"F1.wireOp",EDGE,"E54.MirrorCS"),sQuery(id+"F1.wireOp",EDGE,"E55.MirrorCS"),sQuery(id+"F1.wireOp",EDGE,"E56.MirrorCS"),sQuery(id+"F1.wireOp",EDGE,"E57.MirrorCS"),sQuery(id+"F1.wireOp",EDGE,"E58.MirrorCS"),sQuery(id+"F1.wireOp",EDGE,"E59.MirrorCS"),sQuery(id+"F1.wireOp",EDGE,"E60.MirrorCS"),sQuery(id+"F1.wireOp",EDGE,"E61.MirrorCS"),sQuery(id+"F1.wireOp",EDGE,"E62.MirrorCS"),sQuery(id+"F1.wireOp",EDGE,"E63.MirrorCS"),sQuery(id+"F1.wireOp",EDGE,"E64.MirrorCS"),sQuery(id+"F1.wireOp",EDGE,"E65.MirrorCS"),sQuery(id+"F1.wireOp",EDGE,"E66.MirrorCS"),sQuery(id+"F1.wireOp",EDGE,"E67.MirrorCS"),sQuery(id+"F1.wireOp",EDGE,"E68.MirrorCS"),sQuery(id+"F1.wireOp",EDGE,"E69.MirrorCS"),sQuery(id+"F1.wireOp",EDGE,"E70.MirrorCS"),sQuery(id+"F1.wireOp",EDGE,"E71.MirrorCS"),sQuery(id+"F1.wireOp",EDGE,"E72.MirrorCS"),sQuery(id+"F1.wireOp",EDGE,"E73.MirrorCS"),sQuery(id+"F1.wireOp",EDGE,"E74.MirrorCS")])],"isStart":false});
            var sketch = newSketch(context, id + "F37", { "sketchPlane" : qUnion([Q0])});
            skCircle(sketch, "E92", {"center": v(25, 8.75) * mm, "radius": 2 * mm});
            skCircle(sketch, "E93", {"center": v(38, 8.75) * mm, "radius": 2 * mm});
            skCircle(sketch, "E94", {"center": v(45.5, 16.25) * mm, "radius": 2 * mm});
            skCircle(sketch, "E95", {"center": v(53, 8.75) * mm, "radius": 2 * mm});
            skCircle(sketch, "E96", {"center": v(65, 8.75) * mm, "radius": 2 * mm});
            skSolve(sketch);
        }
        {
            var Q0;
            Q0=makeQuery(id+"F37.imprint","IMPRINT",FACE,{"disambiguationData":[TD([[makeQuery(id+"F37.imprint","IMPRINT",EDGE,{"derivedFrom":sQuery(id+"F37.wireOp",EDGE,"E92")}),1.0]])]});
            var Q1;
            Q1=sQuery(id+"F37.wireOp",EDGE,"E92");
            extrude(context, id + "F38", {"entities" : qUnion([Q0]), "surfaceEntities" : qUnion([Q1]), "oppositeDirection" : true, "depth" : 20 * mm, "offsetDistance" : 25 * mm});
        }
        {
            var Q0;
            Q0=makeQuery(id+"F37.imprint","IMPRINT",FACE,{"disambiguationData":[TD([[makeQuery(id+"F37.imprint","IMPRINT",EDGE,{"derivedFrom":sQuery(id+"F37.wireOp",EDGE,"E93")}),1.0]])]});
            var Q1;
            Q1=sQuery(id+"F37.wireOp",EDGE,"E93");
            extrude(context, id + "F39", {"entities" : qUnion([Q0]), "surfaceEntities" : qUnion([Q1]), "oppositeDirection" : true, "depth" : 20 * mm, "offsetDistance" : 25 * mm});
        }
        {
            var Q0;
            Q0=makeQuery(id+"F37.imprint","IMPRINT",FACE,{"disambiguationData":[TD([[makeQuery(id+"F37.imprint","IMPRINT",EDGE,{"derivedFrom":sQuery(id+"F37.wireOp",EDGE,"E94")}),1.0]])]});
            var Q1;
            Q1=sQuery(id+"F37.wireOp",EDGE,"E94");
            extrude(context, id + "F40", {"entities" : qUnion([Q0]), "surfaceEntities" : qUnion([Q1]), "oppositeDirection" : true, "depth" : 20 * mm, "offsetDistance" : 25 * mm});
        }
        {
            var Q0;
            Q0=makeQuery(id+"F37.imprint","IMPRINT",FACE,{"disambiguationData":[TD([[makeQuery(id+"F37.imprint","IMPRINT",EDGE,{"derivedFrom":sQuery(id+"F37.wireOp",EDGE,"E95")}),1.0]])]});
            extrude(context, id + "F41", {"entities" : qUnion([Q0]), "oppositeDirection" : true, "depth" : 20 * mm, "offsetDistance" : 25 * mm});
        }
        {
            var Q0;
            Q0=makeQuery(id+"F37.imprint","IMPRINT",FACE,{"disambiguationData":[TD([[makeQuery(id+"F37.imprint","IMPRINT",EDGE,{"derivedFrom":sQuery(id+"F37.wireOp",EDGE,"E96")}),1.0]])]});
            extrude(context, id + "F42", {"entities" : qUnion([Q0]), "oppositeDirection" : true, "depth" : 20 * mm, "offsetDistance" : 25 * mm});
        }
        {
            var Q0;
            Q0=makeQuery(id+"F34.opExtrude","CAP_FACE",FACE,{"disambiguationData":[OSD([sQuery(id+"F33.wireOp",EDGE,"E90")])],"isStart":false});
            var sketch = newSketch(context, id + "F43", { "sketchPlane" : qUnion([Q0])});
            skCircle(sketch, "E97", {"center": v(-10, 8.75) * mm, "radius": 4 * mm});
            skSolve(sketch);
        }
        {
            var Q0;
            Q0 = qSketchRegion(id + "F43", true);
            extrude(context, id + "F44", {"entities" : qUnion([Q0]), "operationType" : NewBodyOperationType.ADD, "oppositeDirection" : true, "depth" : 1 * mm, "offsetDistance" : 25 * mm});
        }
        {
            var Q0;
            Q0=makeQuery(id+"F36.opExtrude","CAP_FACE",FACE,{"disambiguationData":[OSD([sQuery(id+"F35.wireOp",EDGE,"E91")])],"isStart":false});
            var sketch = newSketch(context, id + "F45", { "sketchPlane" : qUnion([Q0])});
            skCircle(sketch, "E98", {"center": v(-17.5, 16.25) * mm, "radius": 4 * mm});
            skSolve(sketch);
        }
        {
            var Q0;
            Q0=makeQuery(id+"F45.imprint","IMPRINT",FACE,{"disambiguationData":[TD([[makeQuery(id+"F45.imprint","IMPRINT",EDGE,{"derivedFrom":sQuery(id+"F45.wireOp",EDGE,"E98")}),1.0]])]});
            extrude(context, id + "F46", {"entities" : qUnion([Q0]), "operationType" : NewBodyOperationType.ADD, "oppositeDirection" : true, "depth" : 1 * mm, "offsetDistance" : 25 * mm});
        }
        {
            var Q0;
            Q0=makeQuery(id+"F38.opExtrude","CAP_FACE",FACE,{"disambiguationData":[OSD([sQuery(id+"F37.wireOp",EDGE,"E92")])],"isStart":false});
            var sketch = newSketch(context, id + "F47", { "sketchPlane" : qUnion([Q0])});
            skCircle(sketch, "E99", {"center": v(-25, 8.75) * mm, "radius": 4 * mm});
            skSolve(sketch);
        }
        {
            var Q0;
            Q0=makeQuery(id+"F47.imprint","IMPRINT",FACE,{"disambiguationData":[TD([[makeQuery(id+"F47.imprint","IMPRINT",EDGE,{"derivedFrom":sQuery(id+"F47.wireOp",EDGE,"E99")}),1.0]])]});
            extrude(context, id + "F48", {"entities" : qUnion([Q0]), "operationType" : NewBodyOperationType.ADD, "oppositeDirection" : true, "depth" : 1 * mm, "offsetDistance" : 25 * mm});
        }
        {
            var Q0;
            Q0=makeQuery(id+"F39.opExtrude","CAP_FACE",FACE,{"disambiguationData":[OSD([sQuery(id+"F37.wireOp",EDGE,"E93")])],"isStart":false});
            var sketch = newSketch(context, id + "F49", { "sketchPlane" : qUnion([Q0])});
            skCircle(sketch, "E100", {"center": v(-38, 8.75) * mm, "radius": 4 * mm});
            skSolve(sketch);
        }
        {
            var Q0;
            Q0=makeQuery(id+"F49.imprint","IMPRINT",FACE,{"disambiguationData":[TD([[makeQuery(id+"F49.imprint","IMPRINT",EDGE,{"derivedFrom":sQuery(id+"F49.wireOp",EDGE,"E100")}),1.0]])]});
            extrude(context, id + "F50", {"entities" : qUnion([Q0]), "operationType" : NewBodyOperationType.ADD, "oppositeDirection" : true, "depth" : 1 * mm, "offsetDistance" : 25 * mm});
        }
        {
            var Q0;
            Q0=makeQuery(id+"F40.opExtrude","CAP_FACE",FACE,{"disambiguationData":[OSD([sQuery(id+"F37.wireOp",EDGE,"E94")])],"isStart":false});
            var sketch = newSketch(context, id + "F51", { "sketchPlane" : qUnion([Q0])});
            skCircle(sketch, "E101", {"center": v(-45.5, 16.25) * mm, "radius": 4 * mm});
            skSolve(sketch);
        }
        {
            var Q0;
            Q0=makeQuery(id+"F51.imprint","IMPRINT",FACE,{"disambiguationData":[TD([[makeQuery(id+"F51.imprint","IMPRINT",EDGE,{"derivedFrom":sQuery(id+"F51.wireOp",EDGE,"E101")}),1.0]])]});
            extrude(context, id + "F52", {"entities" : qUnion([Q0]), "operationType" : NewBodyOperationType.ADD, "oppositeDirection" : true, "depth" : 1 * mm, "offsetDistance" : 25 * mm});
        }
        {
            var Q0;
            Q0=makeQuery(id+"F41.opExtrude","CAP_FACE",FACE,{"disambiguationData":[OSD([sQuery(id+"F37.wireOp",EDGE,"E95")])],"isStart":false});
            var sketch = newSketch(context, id + "F53", { "sketchPlane" : qUnion([Q0])});
            skCircle(sketch, "E102", {"center": v(-53, 8.75) * mm, "radius": 4 * mm});
            skSolve(sketch);
        }
        {
            var Q0;
            Q0=makeQuery(id+"F53.imprint","IMPRINT",FACE,{"disambiguationData":[TD([[makeQuery(id+"F53.imprint","IMPRINT",EDGE,{"derivedFrom":sQuery(id+"F53.wireOp",EDGE,"E102")}),1.0]])]});
            extrude(context, id + "F54", {"entities" : qUnion([Q0]), "operationType" : NewBodyOperationType.ADD, "oppositeDirection" : true, "depth" : 1 * mm, "offsetDistance" : 25 * mm});
        }
        {
            var Q0;
            Q0=makeQuery(id+"F42.opExtrude","CAP_FACE",FACE,{"disambiguationData":[OSD([sQuery(id+"F37.wireOp",EDGE,"E96")])],"isStart":false});
            var sketch = newSketch(context, id + "F55", { "sketchPlane" : qUnion([Q0])});
            skCircle(sketch, "E103", {"center": v(-65, 8.75) * mm, "radius": 4 * mm});
            skSolve(sketch);
        }
        {
            var Q0;
            Q0 = qSketchRegion(id + "F55", true);
            extrude(context, id + "F56", {"entities" : qUnion([Q0]), "operationType" : NewBodyOperationType.ADD, "oppositeDirection" : true, "depth" : 1 * mm, "offsetDistance" : 25 * mm});
        }
        {
            var Q0;
            Q0=makeQuery(id+"F2.opExtrude","CAP_FACE",FACE,{"disambiguationData":[OSD([sQuery(id+"F1.wireOp",EDGE,"E38.MirrorCS"),sQuery(id+"F1.wireOp",EDGE,"E39.MirrorCS"),sQuery(id+"F1.wireOp",EDGE,"E40.MirrorCS"),sQuery(id+"F1.wireOp",EDGE,"E41.MirrorCS"),sQuery(id+"F1.wireOp",EDGE,"E42.MirrorCS"),sQuery(id+"F1.wireOp",EDGE,"E43.MirrorCS"),sQuery(id+"F1.wireOp",EDGE,"E44.MirrorCS"),sQuery(id+"F1.wireOp",EDGE,"E45.MirrorCS"),sQuery(id+"F1.wireOp",EDGE,"E46.MirrorCS"),sQuery(id+"F1.wireOp",EDGE,"E47.MirrorCS"),sQuery(id+"F1.wireOp",EDGE,"E48.MirrorCS"),sQuery(id+"F1.wireOp",EDGE,"E49.MirrorCS"),sQuery(id+"F1.wireOp",EDGE,"E50.MirrorCS"),sQuery(id+"F1.wireOp",EDGE,"E51.MirrorCS"),sQuery(id+"F1.wireOp",EDGE,"E52.MirrorCS"),sQuery(id+"F1.wireOp",EDGE,"E53.MirrorCS"),sQuery(id+"F1.wireOp",EDGE,"E54.MirrorCS"),sQuery(id+"F1.wireOp",EDGE,"E55.MirrorCS"),sQuery(id+"F1.wireOp",EDGE,"E56.MirrorCS"),sQuery(id+"F1.wireOp",EDGE,"E57.MirrorCS"),sQuery(id+"F1.wireOp",EDGE,"E58.MirrorCS"),sQuery(id+"F1.wireOp",EDGE,"E59.MirrorCS"),sQuery(id+"F1.wireOp",EDGE,"E60.MirrorCS"),sQuery(id+"F1.wireOp",EDGE,"E61.MirrorCS"),sQuery(id+"F1.wireOp",EDGE,"E62.MirrorCS"),sQuery(id+"F1.wireOp",EDGE,"E63.MirrorCS"),sQuery(id+"F1.wireOp",EDGE,"E64.MirrorCS"),sQuery(id+"F1.wireOp",EDGE,"E65.MirrorCS"),sQuery(id+"F1.wireOp",EDGE,"E66.MirrorCS"),sQuery(id+"F1.wireOp",EDGE,"E67.MirrorCS"),sQuery(id+"F1.wireOp",EDGE,"E68.MirrorCS"),sQuery(id+"F1.wireOp",EDGE,"E69.MirrorCS"),sQuery(id+"F1.wireOp",EDGE,"E70.MirrorCS"),sQuery(id+"F1.wireOp",EDGE,"E71.MirrorCS"),sQuery(id+"F1.wireOp",EDGE,"E72.MirrorCS"),sQuery(id+"F1.wireOp",EDGE,"E73.MirrorCS"),sQuery(id+"F1.wireOp",EDGE,"E74.MirrorCS")])],"isStart":true});
            var sketch = newSketch(context, id + "F57", { "sketchPlane" : qUnion([Q0])});
            skLineSegment(sketch, "E104", {"start": v(0, -10.23) * mm, "end": v(0, 11.81) * mm, "construction": true});
            skLineSegment(sketch, "E105", {"start": v(0, 0) * mm, "end": v(-20.27, 0) * mm, "construction": true});
            skLineSegment(sketch, "E106.bottom", {"start": v(-4, 5) * mm, "end": v(-9, 5) * mm});
            skLineSegment(sketch, "E106.top", {"start": v(-4, -5) * mm, "end": v(-9, -5) * mm});
            skLineSegment(sketch, "E106.left", {"start": v(-4, 5) * mm, "end": v(-4, -5) * mm});
            skLineSegment(sketch, "E106.right", {"start": v(-9, 5) * mm, "end": v(-9, -5) * mm});
            skSolve(sketch);
        }
        {
            var Q0;
            Q0 = qSketchRegion(id + "F57", true);
            extrude(context, id + "F58", {"entities" : qUnion([Q0]), "oppositeDirection" : true, "depth" : 15 * mm, "offsetDistance" : 25 * mm});
        }
        {
            var Q0;
            Q0=makeQuery(id+"F2.opExtrude","CAP_FACE",FACE,{"disambiguationData":[OSD([sQuery(id+"F1.wireOp",EDGE,"E1"),sQuery(id+"F1.wireOp",EDGE,"E2"),sQuery(id+"F1.wireOp",EDGE,"E3.0"),sQuery(id+"F1.wireOp",EDGE,"E4.0"),sQuery(id+"F1.wireOp",EDGE,"E5.0"),sQuery(id+"F1.wireOp",EDGE,"E6.0"),sQuery(id+"F1.wireOp",EDGE,"E7.trimOffspring"),sQuery(id+"F1.wireOp",EDGE,"E8.trimOffspring"),sQuery(id+"F1.wireOp",EDGE,"E9.trimOffspring"),sQuery(id+"F1.wireOp",EDGE,"E10.0"),sQuery(id+"F1.wireOp",EDGE,"E11.0"),sQuery(id+"F1.wireOp",EDGE,"E12.0"),sQuery(id+"F1.wireOp",EDGE,"E13"),sQuery(id+"F1.wireOp",EDGE,"E14.0"),sQuery(id+"F1.wireOp",EDGE,"E15.0"),sQuery(id+"F1.wireOp",EDGE,"E16.trimOffspring"),sQuery(id+"F1.wireOp",EDGE,"E17.0"),sQuery(id+"F1.wireOp",EDGE,"E18.0"),sQuery(id+"F1.wireOp",EDGE,"E19.trimOffspring"),sQuery(id+"F1.wireOp",EDGE,"E20.trimOffspring"),sQuery(id+"F1.wireOp",EDGE,"E21"),sQuery(id+"F1.wireOp",EDGE,"E22.0"),sQuery(id+"F1.wireOp",EDGE,"E23.0"),sQuery(id+"F1.wireOp",EDGE,"E24.0"),sQuery(id+"F1.wireOp",EDGE,"E25.trimOffspring"),sQuery(id+"F1.wireOp",EDGE,"E26.trimOffspring"),sQuery(id+"F1.wireOp",EDGE,"E27.0"),sQuery(id+"F1.wireOp",EDGE,"E28.0"),sQuery(id+"F1.wireOp",EDGE,"E29.trimOffspring"),sQuery(id+"F1.wireOp",EDGE,"E30.0"),sQuery(id+"F1.wireOp",EDGE,"E31.0"),sQuery(id+"F1.wireOp",EDGE,"E32.0"),sQuery(id+"F1.wireOp",EDGE,"E33"),sQuery(id+"F1.wireOp",EDGE,"E34.0"),sQuery(id+"F1.wireOp",EDGE,"E35.0"),sQuery(id+"F1.wireOp",EDGE,"E36.0"),sQuery(id+"F1.wireOp",EDGE,"E37.trimOffspring")])],"isStart":true});
            var sketch = newSketch(context, id + "F59", { "sketchPlane" : qUnion([Q0])});
            skPoint(sketch, "E107.orphan", {"position": v(-65, -8.75) * mm});
            skLineSegment(sketch, "E108.bottom", {"start": v(-67.25, 23) * mm, "end": v(-62.75, 23) * mm});
            skLineSegment(sketch, "E108.top", {"start": v(-67.25, 15) * mm, "end": v(-62.75, 15) * mm});
            skLineSegment(sketch, "E108.left", {"start": v(-67.25, 23) * mm, "end": v(-67.25, 15) * mm});
            skLineSegment(sketch, "E108.right", {"start": v(-62.75, 23) * mm, "end": v(-62.75, 15) * mm});
            skLineSegment(sketch, "E109.MirrorCS", {"start": v(-67.25, -15) * mm, "end": v(-62.75, -15) * mm});
            skLineSegment(sketch, "E110.MirrorCS", {"start": v(-62.75, -23) * mm, "end": v(-62.75, -15) * mm});
            skLineSegment(sketch, "E111.MirrorCS", {"start": v(-67.25, -23) * mm, "end": v(-67.25, -15) * mm});
            skLineSegment(sketch, "E112.MirrorCS", {"start": v(-67.25, -23) * mm, "end": v(-62.75, -23) * mm});
            skSolve(sketch);
        }
        {
            var Q0;
            Q0 = qSketchRegion(id + "F59", true);
            extrude(context, id + "F60", {"entities" : qUnion([Q0]), "oppositeDirection" : true, "depth" : 20 * mm, "offsetDistance" : 25 * mm});
        }
    });
